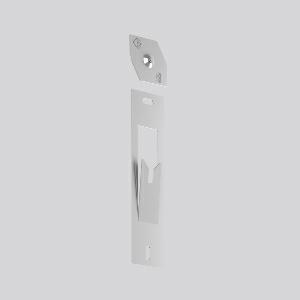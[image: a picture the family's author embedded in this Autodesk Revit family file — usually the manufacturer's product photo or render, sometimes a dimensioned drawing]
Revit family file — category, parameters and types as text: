
# Revit family: linedo_wand_adapter_982814_000_9ddb
name_source: partatom
category: Lighting Fixtures
units: mm (PartAtom-declared; Revit-internal decimal feet)

## family parameters
Cut with Voids When Loaded = No
Host = Face
Light Source = No
Part Type = Normal
Room Calculation Point = No
Round Connector Dimension = Use Diameter
Shared = No

## types (1)
- LINEDO Wand Adapter
    Apparent Load = 0 VA
    Default Elevation = 1800 mm
    Description = Wall mounting made of galvanised sheet steel. For vertical installation of LINEDO luminaire modules. 2 wall suspensions are required per luminaire module (max. 1 x 8 units). With this accessory, the protection type of the luminaire module can be reduced to IP 20.
Colour: unpainted
Length: 200 mm
Width: 53 mm
Height: 9 mm
Weight: 121 g
Type of Installation: Wall (surface)
    Height = 9 mm  [stored 0.0295276 ft]
    Lamp = 0 x
    Length = 200 mm  [stored 0.656168 ft]
    Luminous efficacy = 0 lm/W
    Manufacturer = RZB
    ModVariant = No
    Model = 982814.000
    Mounting Place = Ceiling
    Mounting Type = Surface mounted
    Number of Poles = 1
    OnlyDefault = Yes
    Power Factor = 1
    Product Name = LINEDO Wand Adapter
    Product group = Surface mounted continuous line luminaire system
    ProductGroupID = 310
    Protection Class = Protection class
    Protection Degree = Degree of protection
    RLX_Detail_Level = 1
    RLX_Emergency_Light_Flux = 0 lm
    RLX_Emergency_Type = 0
    RLX_Emergency_Type_DB = No
    RlxData = <blob elided: 10253 chars, md5=5f51bcd1>
    Standby Power = 0 W
    System Light Flux = 0 lm
    System Power = 0 W
    Type Comments = Product without accessories
    Type Image = 982814.000.jpg
    URL = http://relux.com
    VarID = ---
    Voltage = 0 V
    Weight = 0.00 kg
    Width = 53 mm

note: [stored X ft] marks values corroborated as IEEE doubles in the binary element streams (Revit-internal decimal feet)

## geometry (parser evidence)
native form markers: Sweep x11
no freeform markers — native parametric forms only
